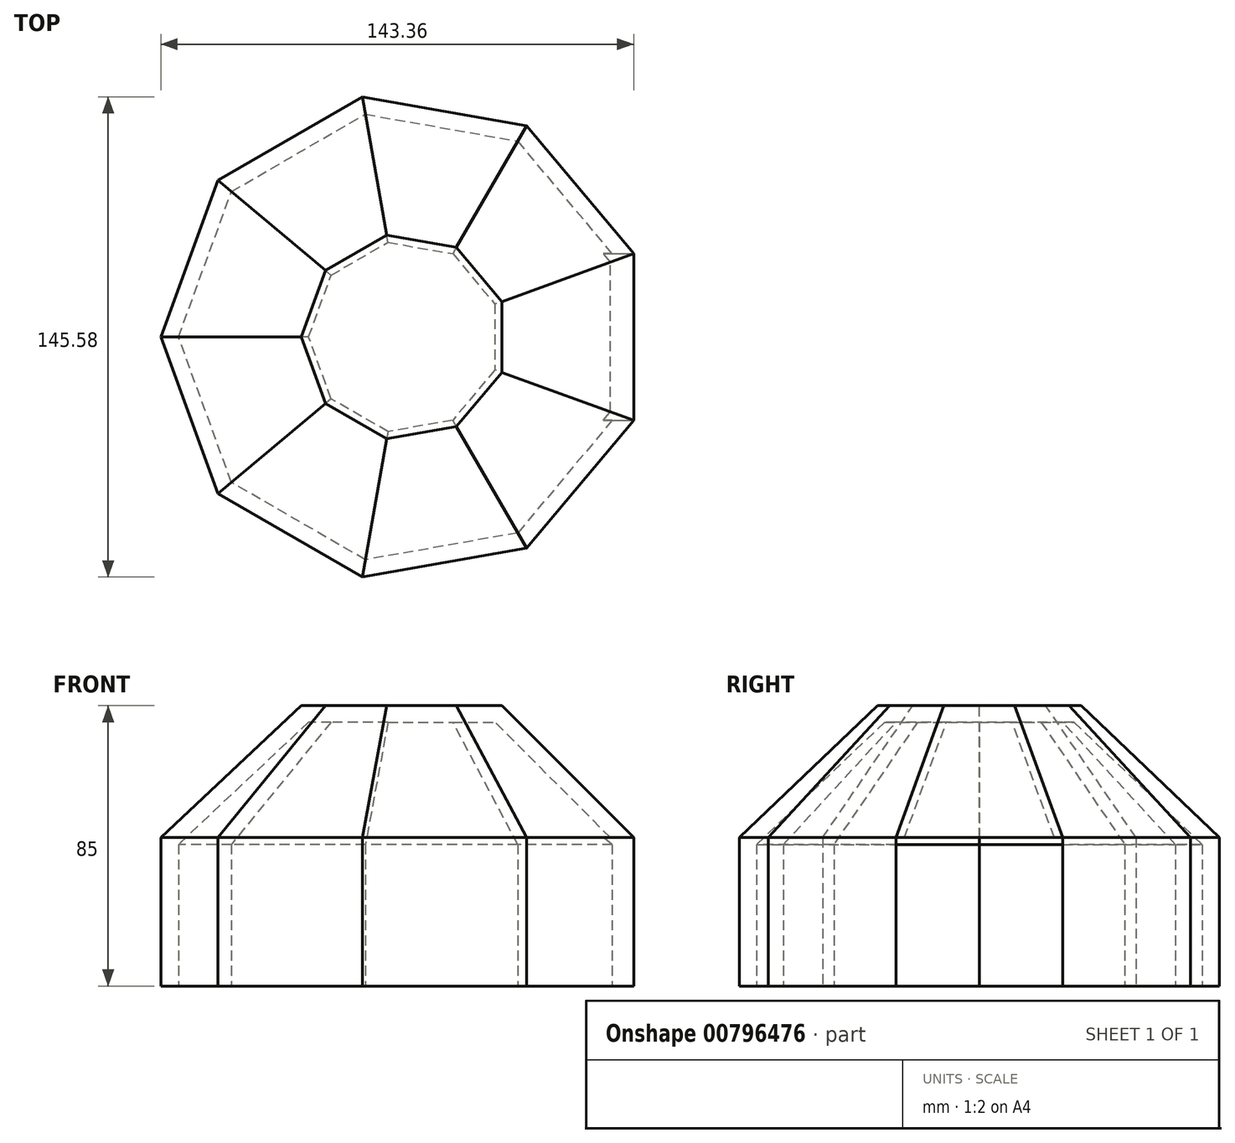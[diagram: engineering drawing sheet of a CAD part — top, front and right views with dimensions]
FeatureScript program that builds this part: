
annotation { "Feature Type Name" : "Feature", "Feature Type Description" : "" }
export const myFeature = defineFeature(function(context is Context, id is Id, definition is map)
    precondition{}
    {
        {
            var Q0;
            Q0=qCreatedBy(makeId("Top.planeOp"),FACE);
            var sketch = newSketch(context, id + "F0", { "sketchPlane" : qUnion([Q0])});
            skCircle(sketch, "E0.cCircle", {"center": v(-73.94, 23.93) * mm, "radius": 69.45 * mm, "construction": true});
            skLineSegment(sketch, "E0.0", {"start": v(-4.49, 49.2) * mm, "end": v(-4.49, -1.35) * mm});
            skLineSegment(sketch, "E0.1", {"start": v(-4.49, -1.35) * mm, "end": v(-36.98, -40.08) * mm});
            skLineSegment(sketch, "E0.2", {"start": v(-36.98, -40.08) * mm, "end": v(-86.77, -48.86) * mm});
            skLineSegment(sketch, "E0.3", {"start": v(-86.77, -48.86) * mm, "end": v(-130.56, -23.58) * mm});
            skLineSegment(sketch, "E0.4", {"start": v(-130.56, -23.58) * mm, "end": v(-147.85, 23.93) * mm});
            skLineSegment(sketch, "E0.5", {"start": v(-147.85, 23.93) * mm, "end": v(-130.56, 71.44) * mm});
            skLineSegment(sketch, "E0.6", {"start": v(-130.56, 71.44) * mm, "end": v(-86.77, 96.72) * mm});
            skLineSegment(sketch, "E0.7", {"start": v(-86.77, 96.72) * mm, "end": v(-36.98, 87.94) * mm});
            skLineSegment(sketch, "E0.8", {"start": v(-36.98, 87.94) * mm, "end": v(-4.49, 49.2) * mm});
            skPoint(sketch, "E0.0.midPoint", {"position": v(-4.49, 23.93) * mm});
            skSolve(sketch);
        }
        {
            var Q0;
            Q0=makeQuery(id+"F0.imprint","IMPRINT",FACE,{"disambiguationData":[TD([[makeQuery(id+"F0.imprint","IMPRINT",EDGE,{"derivedFrom":sQuery(id+"F0.wireOp",EDGE,"E0.0")}),-1.0]])]});
            extrude(context, id + "F1", {"entities" : qUnion([Q0]), "depth" : 85 * mm, "offsetDistance" : 25 * mm});
        }
        {
            var Q0;
            Q0=makeQuery(id+"F1.opExtrude","CAP_FACE",FACE,{"disambiguationData":[OSD([sQuery(id+"F0.wireOp",EDGE,"E0.0"),sQuery(id+"F0.wireOp",EDGE,"E0.1"),sQuery(id+"F0.wireOp",EDGE,"E0.2"),sQuery(id+"F0.wireOp",EDGE,"E0.3"),sQuery(id+"F0.wireOp",EDGE,"E0.4"),sQuery(id+"F0.wireOp",EDGE,"E0.5"),sQuery(id+"F0.wireOp",EDGE,"E0.6"),sQuery(id+"F0.wireOp",EDGE,"E0.7"),sQuery(id+"F0.wireOp",EDGE,"E0.8")])],"isStart":false});
            chamfer(context, id + "F2", {"entities" : qUnion([Q0]), "width" : 40 * mm, "tangentPropagation" : true});
        }
        {
            var Q0;
            Q0=makeQuery(id+"F1.opExtrude","CAP_FACE",FACE,{"disambiguationData":[OSD([sQuery(id+"F0.wireOp",EDGE,"E0.0"),sQuery(id+"F0.wireOp",EDGE,"E0.1"),sQuery(id+"F0.wireOp",EDGE,"E0.2"),sQuery(id+"F0.wireOp",EDGE,"E0.3"),sQuery(id+"F0.wireOp",EDGE,"E0.4"),sQuery(id+"F0.wireOp",EDGE,"E0.5"),sQuery(id+"F0.wireOp",EDGE,"E0.6"),sQuery(id+"F0.wireOp",EDGE,"E0.7"),sQuery(id+"F0.wireOp",EDGE,"E0.8")])],"isStart":true});
            shell(context, id + "F3", {"entities" : qUnion([Q0]), "thickness" : 5 * mm});
        }
        {
            var Q0;
            Q0=makeQuery(id+"F1.opExtrude","SWEPT_FACE",FACE,{"disambiguationData":[OSD([sQuery(id+"F0.wireOp",EDGE,"E0.0")])]});
            var sketch = newSketch(context, id + "F4", { "sketchPlane" : qUnion([Q0])});
            skLineSegment(sketch, "E1.bottom", {"start": v(-1.35, 45) * mm, "end": v(49.2, 45) * mm});
            skLineSegment(sketch, "E1.top", {"start": v(-1.35, 0) * mm, "end": v(49.2, 0) * mm});
            skLineSegment(sketch, "E1.left", {"start": v(-1.35, 45) * mm, "end": v(-1.35, 0) * mm});
            skLineSegment(sketch, "E1.right", {"start": v(49.2, 45) * mm, "end": v(49.2, 0) * mm});
            skSolve(sketch);
        }
        {
            var Q0;
            Q0=makeQuery(id+"F4.imprint","IMPRINT",FACE,{"disambiguationData":[TD([[makeQuery(id+"F4.imprint","IMPRINT",EDGE,{"derivedFrom":sQuery(id+"F4.wireOp",EDGE,"E1.bottom")}),1.0]])]});
            extrude(context, id + "F5", {"entities" : qUnion([Q0]), "operationType" : NewBodyOperationType.REMOVE, "oppositeDirection" : true, "depth" : 70 * mm, "offsetDistance" : 25 * mm});
        }
    });
